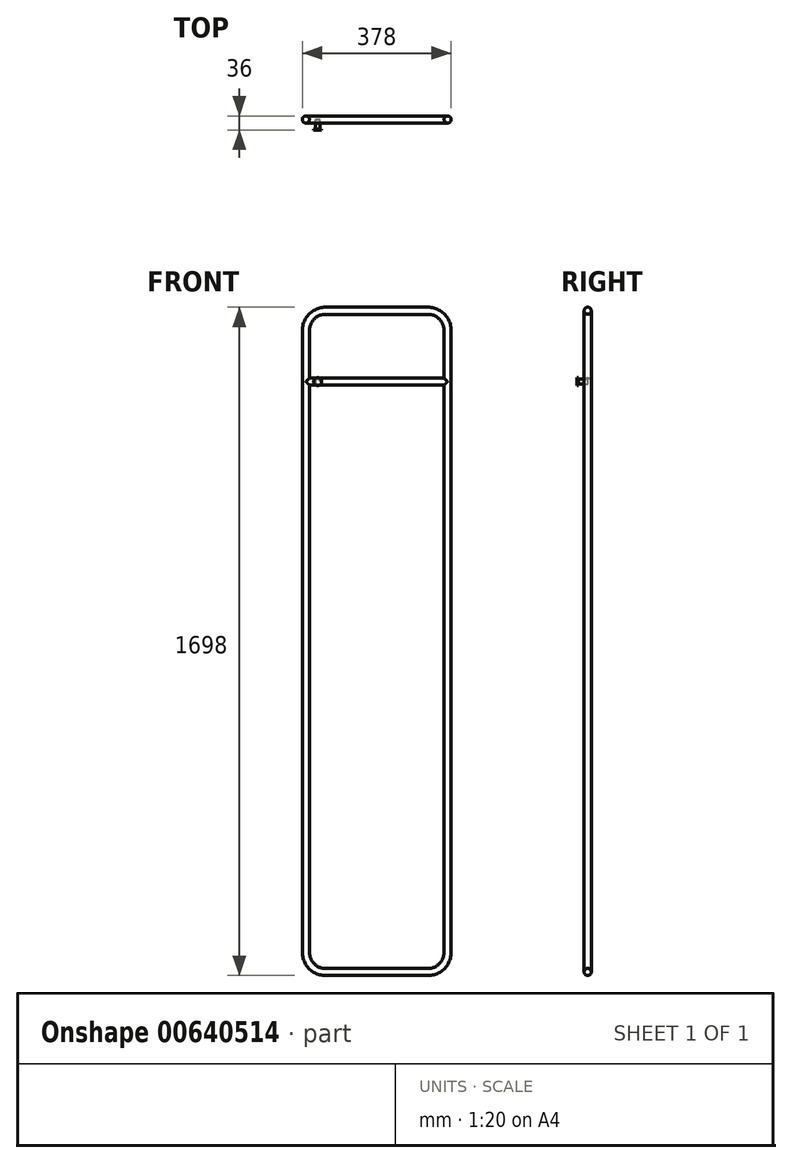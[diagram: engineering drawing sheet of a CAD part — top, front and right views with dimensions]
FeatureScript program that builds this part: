
annotation { "Feature Type Name" : "Feature", "Feature Type Description" : "" }
export const myFeature = defineFeature(function(context is Context, id is Id, definition is map)
    precondition{}
    {
        {
            var Q0;
            Q0=qCreatedBy(makeId("Front.planeOp"),FACE);
            var sketch = newSketch(context, id + "F0", { "sketchPlane" : qUnion([Q0])});
            skLineSegment(sketch, "E0", {"start": v(0, 0) * mm, "end": v(0, 1680) * mm, "construction": true});
            skLineSegment(sketch, "E1", {"start": v(0, 1680) * mm, "end": v(0, 1500) * mm, "construction": true});
            skSolve(sketch);
        }
        {
            var Q0;
            Q0=qCreatedBy(makeId("Front.planeOp"),FACE);
            var sketch = newSketch(context, id + "F1", { "sketchPlane" : qUnion([Q0])});
            skLineSegment(sketch, "E2.bottom", {"start": v(180, 0) * mm, "end": v(-180, 0) * mm, "construction": true});
            skLineSegment(sketch, "E2.top", {"start": v(180, 1680) * mm, "end": v(-180, 1680) * mm, "construction": true});
            skLineSegment(sketch, "E2.left", {"start": v(180, 0) * mm, "end": v(180, 1680) * mm, "construction": true});
            skLineSegment(sketch, "E2.right", {"start": v(-180, 0) * mm, "end": v(-180, 1680) * mm, "construction": true});
            skPoint(sketch, "E2.middle", {"position": v(0, 840) * mm});
            skLineSegment(sketch, "E3.bottom", {"start": v(-130, 1680) * mm, "end": v(130, 1680) * mm});
            skLineSegment(sketch, "E3.top", {"start": v(-130, 0) * mm, "end": v(130, 0) * mm});
            skLineSegment(sketch, "E3.left", {"start": v(-180, 1630) * mm, "end": v(-180, 50) * mm});
            skLineSegment(sketch, "E3.right", {"start": v(180, 1630) * mm, "end": v(180, 50) * mm});
            skPoint(sketch, "E4.visualSharp", {"position": v(-180, 1680) * mm});
            skArc(sketch, "E4.filletArc", {"start": v(-130, 1680) * mm, "mid": v(-165.36, 1665.36) * mm, "end": v(-180, 1630) * mm});
            skPoint(sketch, "E5.visualSharp", {"position": v(180, 1680) * mm});
            skArc(sketch, "E5.filletArc", {"start": v(180, 1630) * mm, "mid": v(165.36, 1665.36) * mm, "end": v(130, 1680) * mm});
            skPoint(sketch, "E6.visualSharp", {"position": v(180, 0) * mm});
            skArc(sketch, "E6.filletArc", {"start": v(130, 0) * mm, "mid": v(165.36, 14.64) * mm, "end": v(180, 50) * mm});
            skPoint(sketch, "E7.visualSharp", {"position": v(-180, 0) * mm});
            skArc(sketch, "E7.filletArc", {"start": v(-180, 50) * mm, "mid": v(-165.36, 14.64) * mm, "end": v(-130, 0) * mm});
            skLineSegment(sketch, "E8", {"start": v(0, 1680) * mm, "end": v(0, 1500) * mm, "construction": true});
            skLineSegment(sketch, "E9", {"start": v(-180, 1500) * mm, "end": v(180, 1500) * mm});
            skSolve(sketch);
        }
        {
            var Q0;
            Q0=qCreatedBy(makeId("Right.planeOp"),FACE);
            var sketch = newSketch(context, id + "F2", { "sketchPlane" : qUnion([Q0])});
            skCircle(sketch, "E10", {"center": v(0, 0) * mm, "radius": 9 * mm});
            skCircle(sketch, "E11", {"center": v(0, 1500) * mm, "radius": 9 * mm});
            skSolve(sketch);
        }
        {
            var Q0;
            Q0=makeQuery(id+"F2.imprint","IMPRINT",FACE,{"disambiguationData":[TD([[makeQuery(id+"F2.imprint","IMPRINT",EDGE,{"derivedFrom":sQuery(id+"F2.wireOp",EDGE,"E10")}),1.0]])]});
            var Q1;
            Q1=sQuery(id+"F1.wireOp",EDGE,"E3.top");
            var Q2;
            Q2=sQuery(id+"F1.wireOp",EDGE,"E6.filletArc");
            var Q3;
            Q3=sQuery(id+"F1.wireOp",EDGE,"E3.right");
            var Q4;
            Q4=sQuery(id+"F1.wireOp",EDGE,"E5.filletArc");
            var Q5;
            Q5=sQuery(id+"F1.wireOp",EDGE,"E3.bottom");
            var Q6;
            Q6=sQuery(id+"F1.wireOp",EDGE,"E4.filletArc");
            var Q7;
            Q7=sQuery(id+"F1.wireOp",EDGE,"E3.left");
            var Q8;
            Q8=sQuery(id+"F1.wireOp",EDGE,"E7.filletArc");
            sweep(context, id + "F3", {"profiles" : qUnion([Q0]), "path" : qUnion([Q1, Q2, Q3, Q4, Q5, Q6, Q7, Q8])});
        }
        {
            var Q0;
            Q0=makeQuery(id+"F2.imprint","IMPRINT",FACE,{"disambiguationData":[TD([[makeQuery(id+"F2.imprint","IMPRINT",EDGE,{"derivedFrom":sQuery(id+"F2.wireOp",EDGE,"E11")}),1.0]])]});
            var Q1;
            Q1=sQuery(id+"F1.wireOp",EDGE,"E9");
            sweep(context, id + "F4", {"operationType" : NewBodyOperationType.ADD, "profiles" : qUnion([Q0]), "path" : qUnion([Q1])});
        }
        {
            var Q0;
            Q0=qCreatedBy(makeId("Front.planeOp"),FACE);
            var sketch = newSketch(context, id + "F5", { "sketchPlane" : qUnion([Q0])});
            skCircle(sketch, "E12", {"center": v(-150, 1500) * mm, "radius": 6 * mm});
            skSolve(sketch);
        }
        {
            var Q0;
            Q0 = qSketchRegion(id + "F5", true);
            extrude(context, id + "F6", {"entities" : qUnion([Q0]), "depth" : 24 * mm, "offsetDistance" : 25 * mm});
        }
        {
            var Q0;
            Q0=makeQuery(id+"F6.opExtrude","CAP_FACE",FACE,{"disambiguationData":[OSD([sQuery(id+"F5.wireOp",EDGE,"E12")])],"isStart":false});
            var sketch = newSketch(context, id + "F7", { "sketchPlane" : qUnion([Q0])});
            skCircle(sketch, "E13", {"center": v(-150, 1500) * mm, "radius": 10 * mm});
            skSolve(sketch);
        }
        {
            var Q0;
            Q0 = qSketchRegion(id + "F7", true);
            extrude(context, id + "F8", {"entities" : qUnion([Q0]), "operationType" : NewBodyOperationType.ADD, "depth" : 3 * mm, "offsetDistance" : 25 * mm});
        }
    });
